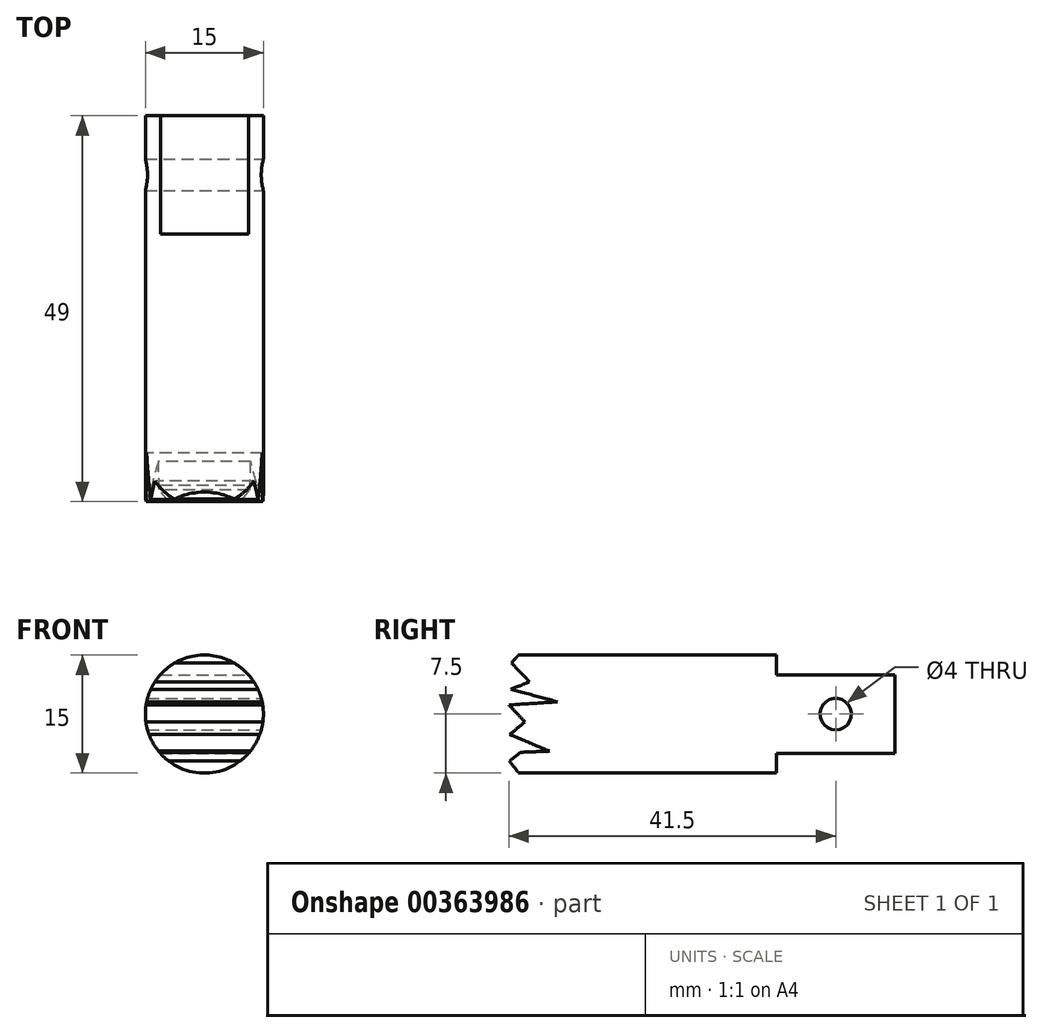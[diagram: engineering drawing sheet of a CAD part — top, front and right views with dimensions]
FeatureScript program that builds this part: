
annotation { "Feature Type Name" : "Feature", "Feature Type Description" : "" }
export const myFeature = defineFeature(function(context is Context, id is Id, definition is map)
    precondition{}
    {
        {
            var Q0;
            Q0=qCreatedBy(makeId("Front.planeOp"),FACE);
            var sketch = newSketch(context, id + "F0", { "sketchPlane" : qUnion([Q0])});
            skCircle(sketch, "E0", {"center": v(0, 0) * mm, "radius": 7.5 * mm});
            skSolve(sketch);
        }
        {
            var Q0;
            Q0=makeQuery(id+"F0.imprint","IMPRINT",FACE,{"disambiguationData":[TD([[makeQuery(id+"F0.imprint","IMPRINT",EDGE,{"derivedFrom":sQuery(id+"F0.wireOp",EDGE,"E0")}),1.0]])]});
            extrude(context, id + "F1", {"entities" : qUnion([Q0]), "depth" : 50 * mm});
        }
        {
            var Q0;
            Q0=qCreatedBy(makeId("Right.planeOp"),FACE);
            var sketch = newSketch(context, id + "F2", { "sketchPlane" : qUnion([Q0])});
            skLineSegment(sketch, "E1", {"start": v(-51.26, 11.15) * mm, "end": v(-44.57, 11.15) * mm});
            skLineSegment(sketch, "E2", {"start": v(-44.57, 11.15) * mm, "end": v(-48.7, 6.48) * mm});
            skLineSegment(sketch, "E3", {"start": v(-48.7, 6.48) * mm, "end": v(-46.39, 4.1) * mm});
            skLineSegment(sketch, "E4", {"start": v(-46.39, 4.1) * mm, "end": v(-48.77, 3.14) * mm});
            skLineSegment(sketch, "E5", {"start": v(-48.77, 3.14) * mm, "end": v(-42.82, 1.55) * mm});
            skLineSegment(sketch, "E6", {"start": v(-42.82, 1.55) * mm, "end": v(-49, 1.15) * mm});
            skLineSegment(sketch, "E7", {"start": v(-49, 1.15) * mm, "end": v(-46.98, -0.99) * mm});
            skLineSegment(sketch, "E8", {"start": v(-46.98, -0.99) * mm, "end": v(-48.91, -2.6) * mm});
            skLineSegment(sketch, "E9", {"start": v(-48.91, -2.6) * mm, "end": v(-43.88, -4.7) * mm});
            skLineSegment(sketch, "E10", {"start": v(-43.88, -4.7) * mm, "end": v(-47.53, -4.85) * mm});
            skLineSegment(sketch, "E11", {"start": v(-47.53, -4.85) * mm, "end": v(-48.95, -5.98) * mm});
            skLineSegment(sketch, "E12", {"start": v(-48.95, -5.98) * mm, "end": v(-47, -8.42) * mm});
            skLineSegment(sketch, "E13", {"start": v(-47, -8.42) * mm, "end": v(-51.26, -8.58) * mm});
            skLineSegment(sketch, "E14", {"start": v(-51.26, -8.58) * mm, "end": v(-51.26, 11.15) * mm});
            skSolve(sketch);
        }
        {
            var Q0;
            Q0=makeQuery(id+"F2.imprint","IMPRINT",FACE,{"disambiguationData":[TD([[makeQuery(id+"F2.imprint","IMPRINT",EDGE,{"derivedFrom":sQuery(id+"F2.wireOp",EDGE,"E1")}),-1.0]])]});
            extrude(context, id + "F3", {"entities" : qUnion([Q0]), "operationType" : NewBodyOperationType.REMOVE, "endBound" : BoundingType.SYMMETRIC, "depth" : 25 * mm});
        }
        {
            var Q0;
            Q0=qCreatedBy(makeId("Front.planeOp"),FACE);
            var sketch = newSketch(context, id + "F4", { "sketchPlane" : qUnion([Q0])});
            skLineSegment(sketch, "E15.bottom", {"start": v(-7.5, -5) * mm, "end": v(7.5, -5) * mm});
            skLineSegment(sketch, "E15.top", {"start": v(-7.5, 5) * mm, "end": v(7.5, 5) * mm});
            skPoint(sketch, "E15.middle", {"position": v(0, 0) * mm});
            skLineSegment(sketch, "E16", {"start": v(-7.5, 5) * mm, "end": v(-7.5, 9.14) * mm});
            skLineSegment(sketch, "E17", {"start": v(-7.5, 9.14) * mm, "end": v(7.5, 9.14) * mm});
            skLineSegment(sketch, "E18", {"start": v(7.5, 9.14) * mm, "end": v(7.5, 5) * mm});
            skLineSegment(sketch, "E19", {"start": v(-7.5, -5) * mm, "end": v(-7.5, -12.74) * mm});
            skLineSegment(sketch, "E20", {"start": v(-7.5, -12.74) * mm, "end": v(7.5, -12.74) * mm});
            skLineSegment(sketch, "E21", {"start": v(7.5, -12.74) * mm, "end": v(7.5, -5) * mm});
            skSolve(sketch);
        }
        {
            var Q0;
            Q0=makeQuery(id+"F4.imprint","IMPRINT",FACE,{"disambiguationData":[TD([[makeQuery(id+"F4.imprint","IMPRINT",EDGE,{"derivedFrom":sQuery(id+"F4.wireOp",EDGE,"E15.bottom")}),-1.0]])]});
            var Q1;
            Q1=makeQuery(id+"F4.imprint","IMPRINT",FACE,{"disambiguationData":[TD([[makeQuery(id+"F4.imprint","IMPRINT",EDGE,{"derivedFrom":sQuery(id+"F4.wireOp",EDGE,"E15.top")}),1.0]])]});
            extrude(context, id + "F5", {"entities" : qUnion([Q0, Q1]), "operationType" : NewBodyOperationType.REMOVE, "depth" : 15 * mm});
        }
        {
            var Q0;
            Q0=qCreatedBy(makeId("Right.planeOp"),FACE);
            var sketch = newSketch(context, id + "F6", { "sketchPlane" : qUnion([Q0])});
            skCircle(sketch, "E22", {"center": v(-7.5, 0) * mm, "radius": 2 * mm});
            skSolve(sketch);
        }
        {
            var Q0;
            Q0 = qSketchRegion(id + "F6", true);
            extrude(context, id + "F7", {"entities" : qUnion([Q0]), "operationType" : NewBodyOperationType.REMOVE, "endBound" : BoundingType.SYMMETRIC, "oppositeDirection" : true, "depth" : 25 * mm});
        }
    });
